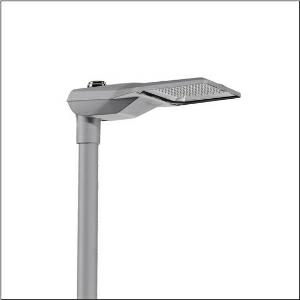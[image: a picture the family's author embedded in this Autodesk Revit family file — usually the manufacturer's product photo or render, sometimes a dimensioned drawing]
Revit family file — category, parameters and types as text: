
# Revit family: streetlight_sl_21_midi___p0_8a_5xe7u27n08nb_7872
name_source: partatom
category: Lighting Fixtures
units: mm (PartAtom-declared; Revit-internal decimal feet)

## family parameters
Cut with Voids When Loaded = No
Host = Face
Light Source = No
Part Type = Normal
Room Calculation Point = No
Round Connector Dimension = Use Diameter
Shared = No

## types (1)
- --- (1 x LED, 18940 lm, 151.2 W, 2200K)
    Apparent Load = 151 VA
    CIE Flux Codes = 36 69 97 100 100
    Color Rendering = 70
    Color Temperature = 2200K
    Default Elevation = 1800 mm
    Description = Streetlight SL 21 midi, mast luminaire, primary light control with lens, of PMMA, primary optical cover: cover, of toughened safety glass, transparent, light distribution: P0.8a, light emission: direct distribution, primary light characteristic: asymmetric, installation type: side-entry, LED, 3G 2.5mm², High Power LED, rated luminous flux: 18.940lm, luminous efficacy: 125lm/W, light colour: 722, colour temperature: 2200K, control gear: NEMA (7pin), control: flexible luminous flux parameterisation, time-dependent luminous flux control, constant luminous flux control, pre-setting: linear dimming characteristic, overheat protection, mains connection: 220..240V, AC, 50/60Hz, connection cable pre-assembled, cable length: 12,5m, wiring characteristics: H05VV-F, start of lifetime: 151W, end of service life: 157W, reduction: 70W, luminaire housing, of diecast aluminium (EN AC-44300), powder-coated, Siteco® metallic grey (DB 702S), corrosivity category C5 mid according to DIN EN ISO 12944, multi-level sealing system, sealing non-destructively replaceable, inclination adjustable: 0°, 5°, 10°, 15°, length: 644mm, width: 335mm, height: 110mm, spigot size: 42mm (side-entry), mounting height: 4..8m, protection rating (complete): IP66, insulation class (complete): insulation class I (protective earthing), certification: CE, ENEC, ENEC+, VDE, impact resistance: IK09, permissible operating ambient temperature for outdoor applications: -40..+50°C, standard-compliant lighting for roads and squares, packaging unit: 1 piece

Light Distribution: P0.8a
    Height = 111 mm
    Lamp = 1 x LED
    Lamp Light Flux = 18940 lm
    Lamp Power = 151.2 W
    Lamp count = 1
    Length = 644 mm
    Luminous efficacy = 125 lm/W
    Manufacturer = Siteco
    ModVariant = No
    Model = 5XE7U27N08NB
    Number of Poles = 1
    OnlyDefault = Yes
    Power Factor = 1
    Product Name = Streetlight SL 21 midi | P0.8a
    Product group = mast luminaire | pylon top
    ProductGroupID = 6100
    Protection Class = Protection class I
    Protection Degree = IP 66
    RLX_Detail_Level = 1
    RLX_Emergency_Light_Flux = 0 lm
    RLX_Emergency_Type = 0
    RLX_Emergency_Type_DB = No
    RlxData = <blob elided: 90133 chars, md5=d1d653b4>
    Socket = socket
    Standby Power = 0 W
    System Light Flux = 18939 lm
    System Power = 151 W
    Type Comments = factory setting: luminous flux: 100 % | dim-lin: 254 | 802 mA
    Type Image = l_1294377.jpg
    URL = http://relux.com
    VarID = @adj_068754
    Voltage = 0 V
    Weight = 0.00 kg
    Width = 336 mm

## geometry (parser evidence)
native form markers: Blend x4, Sweep x12
no freeform markers — native parametric forms only
